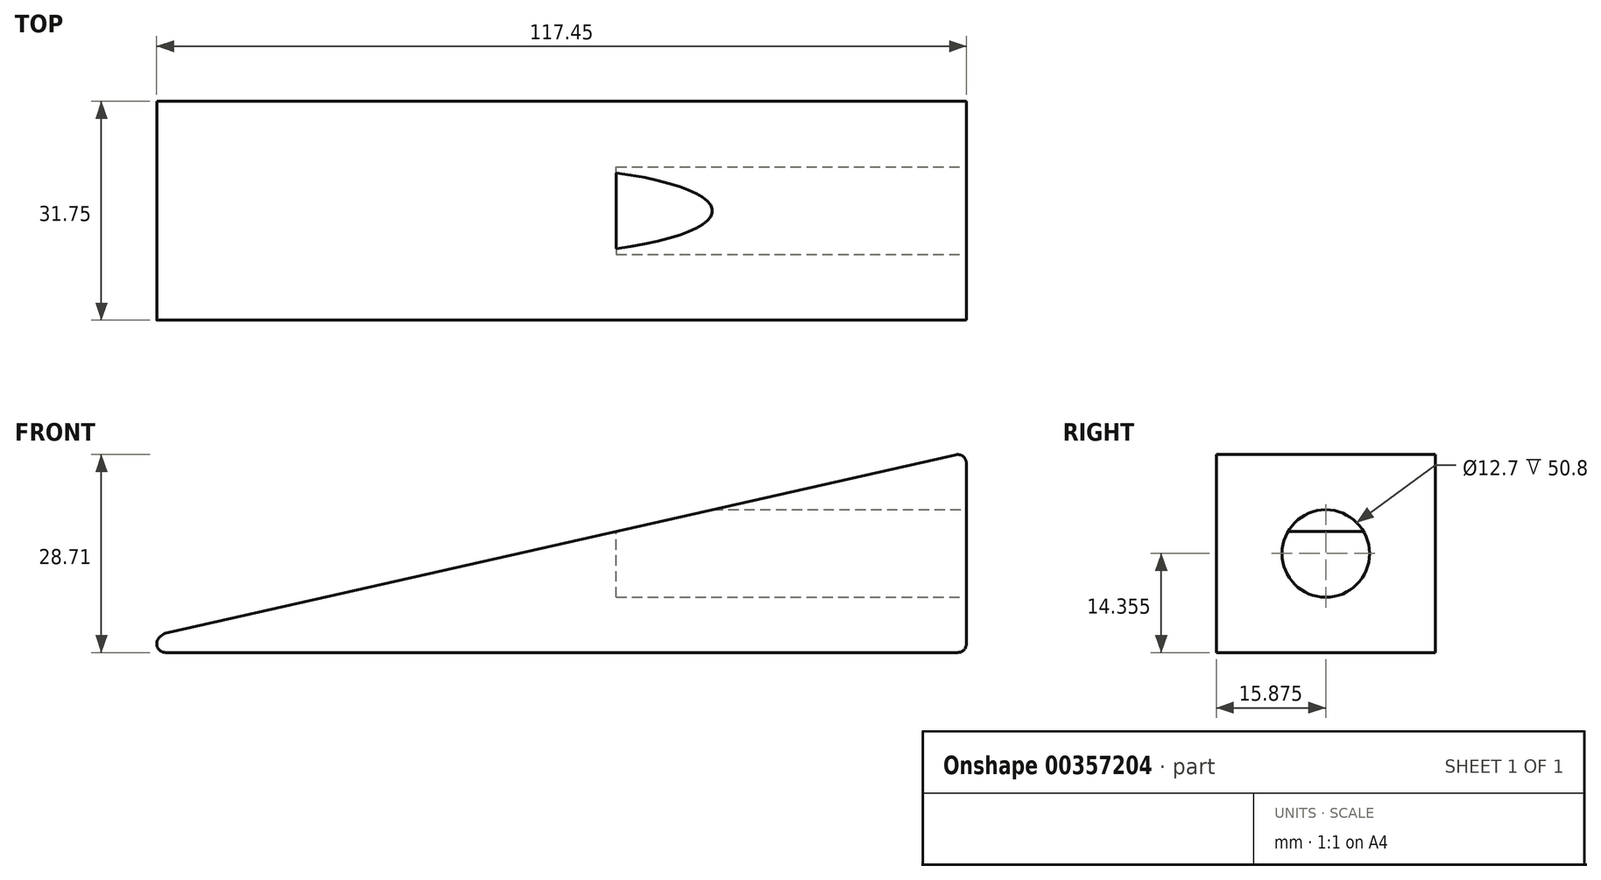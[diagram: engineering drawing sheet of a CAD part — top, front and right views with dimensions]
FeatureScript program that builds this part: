
annotation { "Feature Type Name" : "Feature", "Feature Type Description" : "" }
export const myFeature = defineFeature(function(context is Context, id is Id, definition is map)
    precondition{}
    {
        {
            var Q0;
            Q0=qCreatedBy(makeId("Front.planeOp"),FACE);
            var sketch = newSketch(context, id + "F0", { "sketchPlane" : qUnion([Q0])});
            skLineSegment(sketch, "E0", {"start": v(-64.59, 0) * mm, "end": v(51.59, 0) * mm});
            skLineSegment(sketch, "E1", {"start": v(51.59, 0) * mm, "end": v(51.59, 27.44) * mm});
            skLineSegment(sketch, "E2", {"start": v(50.04, 28.68) * mm, "end": v(-64.72, 2.74) * mm});
            skArc(sketch, "E3", {"start": v(-64.75, 2.72) * mm, "mid": v(-65.12, 2.48) * mm, "end": v(-65.46, 2.2) * mm});
            skPoint(sketch, "E4.visualSharp", {"position": v(-64.74, 2.73) * mm});
            skArc(sketch, "E4.filletArc", {"start": v(-64.72, 2.74) * mm, "mid": v(-64.74, 2.73) * mm, "end": v(-64.75, 2.72) * mm});
            skPoint(sketch, "E5.visualSharp", {"position": v(-66.6, 0) * mm});
            skArc(sketch, "E5.filletArc", {"start": v(-65.46, 2.2) * mm, "mid": v(-65.76, 0.8) * mm, "end": v(-64.59, 0) * mm});
            skPoint(sketch, "E6.visualSharp", {"position": v(51.59, 29.03) * mm});
            skArc(sketch, "E6.filletArc", {"start": v(51.59, 27.44) * mm, "mid": v(51.1, 28.43) * mm, "end": v(50.04, 28.68) * mm});
            skSolve(sketch);
        }
        {
            var Q0;
            Q0 = qSketchRegion(id + "F0", true);
            extrude(context, id + "F1", {"entities" : qUnion([Q0]), "depth" : 31.75 * mm});
        }
        {
            var Q0;
            Q0=makeQuery(id+"F1.opExtrude","SWEPT_EDGE",EDGE,{"disambiguationData":[OSD([sQuery(id+"F0.wireOp",EDGE,"E0"),sQuery(id+"F0.wireOp",EDGE,"E1")])]});
            fillet(context, id + "F2", {"entities" : qUnion([Q0]), "radius" : 1.27 * mm, "tangentPropagation" : true, "allowEdgeOverflow" : false});
        }
        {
            var Q0;
            Q0=makeQuery(id+"F1.opExtrude","SWEPT_FACE",FACE,{"disambiguationData":[OSD([sQuery(id+"F0.wireOp",EDGE,"E1")])]});
            var sketch = newSketch(context, id + "F3", { "sketchPlane" : qUnion([Q0])});
            skCircle(sketch, "E7", {"center": v(-15.88, 14.36) * mm, "radius": 6.35 * mm});
            skPoint(sketch, "E7.centerSnap0", {"position": v(-31.75, 14.36) * mm});
            skPoint(sketch, "E7.centerSnap1", {"position": v(-15.88, 1.27) * mm});
            skSolve(sketch);
        }
        {
            var Q0;
            Q0 = qSketchRegion(id + "F3", true);
            extrude(context, id + "F4", {"entities" : qUnion([Q0]), "operationType" : NewBodyOperationType.REMOVE, "oppositeDirection" : true, "depth" : 50.8 * mm});
        }
    });
